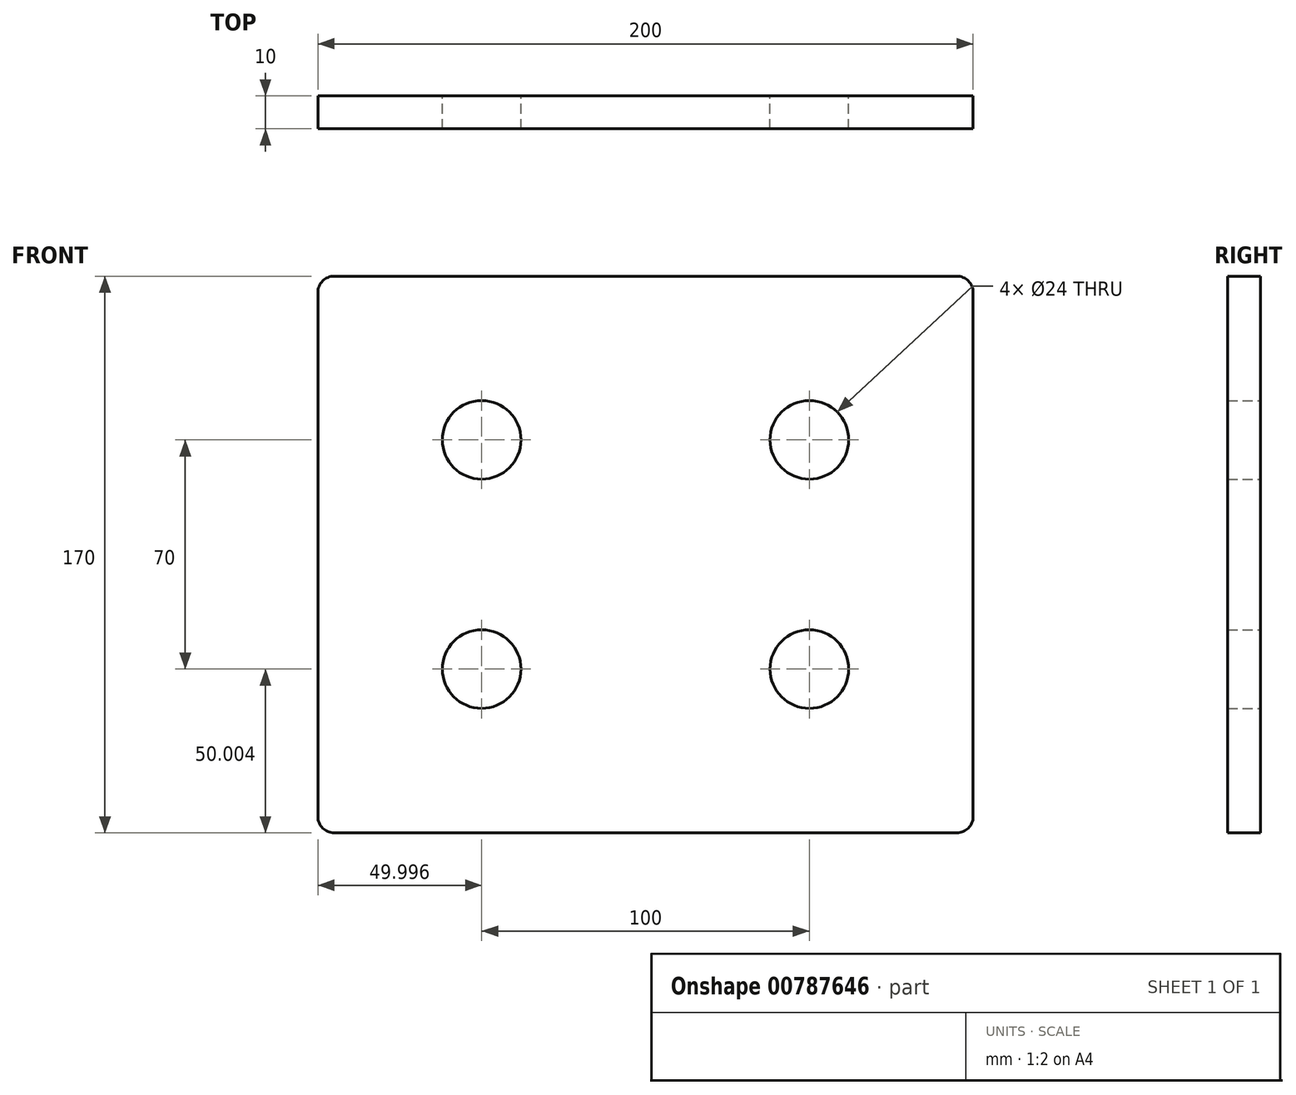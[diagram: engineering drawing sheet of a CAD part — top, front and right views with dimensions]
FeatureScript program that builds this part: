
annotation { "Feature Type Name" : "Feature", "Feature Type Description" : "" }
export const myFeature = defineFeature(function(context is Context, id is Id, definition is map)
    precondition{}
    {
        {
            var Q0;
            Q0=qCreatedBy(makeId("Front.planeOp"),FACE);
            var sketch = newSketch(context, id + "F0", { "sketchPlane" : qUnion([Q0])});
            skLineSegment(sketch, "E0.bottom", {"start": v(-109.22, 42.18) * mm, "end": v(80.78, 42.18) * mm});
            skLineSegment(sketch, "E0.top", {"start": v(-109.22, -127.82) * mm, "end": v(80.78, -127.82) * mm});
            skLineSegment(sketch, "E0.left", {"start": v(-114.22, 37.18) * mm, "end": v(-114.22, -122.82) * mm});
            skLineSegment(sketch, "E0.right", {"start": v(85.78, 37.18) * mm, "end": v(85.78, -122.82) * mm});
            skPoint(sketch, "E1.visualSharp", {"position": v(-114.22, 42.18) * mm});
            skArc(sketch, "E1.filletArc", {"start": v(-109.22, 42.18) * mm, "mid": v(-112.76, 40.72) * mm, "end": v(-114.22, 37.18) * mm});
            skPoint(sketch, "E2.visualSharp", {"position": v(85.78, 42.18) * mm});
            skArc(sketch, "E2.filletArc", {"start": v(85.78, 37.18) * mm, "mid": v(84.31, 40.72) * mm, "end": v(80.78, 42.18) * mm});
            skPoint(sketch, "E3.visualSharp", {"position": v(85.78, -127.82) * mm});
            skArc(sketch, "E3.filletArc", {"start": v(80.78, -127.82) * mm, "mid": v(84.31, -126.35) * mm, "end": v(85.78, -122.82) * mm});
            skPoint(sketch, "E4.visualSharp", {"position": v(-114.22, -127.82) * mm});
            skArc(sketch, "E4.filletArc", {"start": v(-114.22, -122.82) * mm, "mid": v(-112.76, -126.35) * mm, "end": v(-109.22, -127.82) * mm});
            skLineSegment(sketch, "E5", {"start": v(-14.22, 42.18) * mm, "end": v(-14.22, -127.82) * mm, "construction": true});
            skLineSegment(sketch, "E6", {"start": v(35.78, 42.18) * mm, "end": v(35.78, -127.82) * mm, "construction": true});
            skCircle(sketch, "E7", {"center": v(35.78, -7.82) * mm, "radius": 12 * mm});
            skCircle(sketch, "E8", {"center": v(35.78, -77.82) * mm, "radius": 12 * mm});
            skCircle(sketch, "E9.MirrorC", {"center": v(-64.22, -7.82) * mm, "radius": 12 * mm});
            skCircle(sketch, "E10.MirrorC", {"center": v(-64.22, -77.82) * mm, "radius": 12 * mm});
            skSolve(sketch);
        }
        {
            var Q0;
            Q0 = qSketchRegion(id + "F0", true);
            extrude(context, id + "F1", {"entities" : qUnion([Q0]), "depth" : 10 * mm, "offsetDistance" : 25 * mm});
        }
    });
